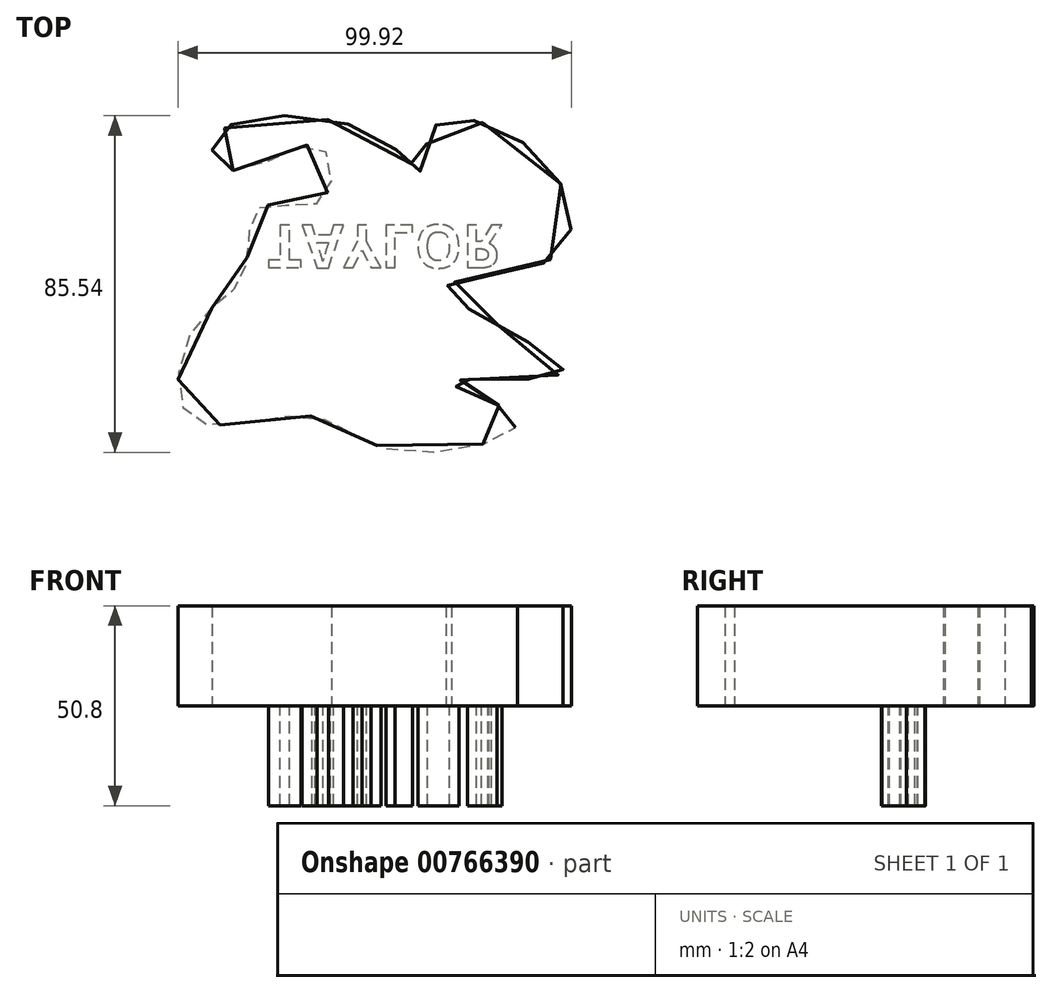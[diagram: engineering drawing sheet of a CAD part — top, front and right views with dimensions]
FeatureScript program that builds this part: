
annotation { "Feature Type Name" : "Feature", "Feature Type Description" : "" }
export const myFeature = defineFeature(function(context is Context, id is Id, definition is map)
    precondition{}
    {
        {
            var Q0;
            Q0=qCreatedBy(makeId("Top.planeOp"),FACE);
            var sketch = newSketch(context, id + "F0", { "sketchPlane" : qUnion([Q0])});
            skFitSpline(sketch, "E0", {"points": [v(-38.96, 34.8) * mm, v(-16.97, 40.86) * mm, v(-16.59, 27.02) * mm, v(-32.52, 25.12) * mm, v(-36.3, 8.25) * mm, v(-48.82, -5.02) * mm, v(-49.58, -28.16) * mm, v(-19.62, -27.59) * mm, v(2.94, -36.5) * mm, v(33.08, -28.53) * mm, v(16.59, -19.05) * mm, v(44.84, -16.21) * mm, v(15.26, 4.27) * mm, v(42.37, 12.6) * mm, v(39.15, 38.2) * mm, v(12.04, 45.79) * mm, v(9.39, 34.6) * mm, v(-3.89, 44.27) * mm, v(-43.51, 43.32) * mm, v(-38.96, 34.8) * mm]});
            skSolve(sketch);
        }
        {
            var Q0;
            Q0=makeQuery(id+"F0.imprint","IMPRINT",FACE,{"disambiguationData":[TD([[makeQuery(id+"F0.imprint","IMPRINT",EDGE,{"derivedFrom":sQuery(id+"F0.wireOp",EDGE,"E0")}),1.0]])]});
            extrude(context, id + "F1", {"entities" : qUnion([Q0]), "depth" : 25.4 * mm, "offsetDistance" : 25.4 * mm});
        }
        {
            var Q0;
            Q0=makeQuery(id+"F1.opExtrude","CAP_FACE",FACE,{"disambiguationData":[OSD([sQuery(id+"F0.wireOp",EDGE,"E0")])],"isStart":true});
            var sketch = newSketch(context, id + "F2", { "sketchPlane" : qUnion([Q0])});
            skText(sketch, "E1", { "text": "T", "fontName": "OpenSans-Bold.ttf"});
            const initialGuessF2  = {"E1": [-0.00813, -0.02705, 1, 0, 0.01205]};
            skSetInitialGuess(sketch, initialGuessF2);
            skSolve(sketch);
        }
        {
            var Q0;
            Q0 = qSketchRegion(id + "F2", true);
            extrude(context, id + "F3", {"entities" : qUnion([Q0]), "operationType" : NewBodyOperationType.ADD, "oppositeDirection" : true, "depth" : 25.4 * mm, "offsetDistance" : 25.4 * mm});
        }
        {
            var Q0;
            Q0=makeQuery(id+"F1.opExtrude","CAP_FACE",FACE,{"disambiguationData":[OSD([sQuery(id+"F0.wireOp",EDGE,"E0")])],"isStart":true});
            var sketch = newSketch(context, id + "F4", { "sketchPlane" : qUnion([Q0])});
            skText(sketch, "E2", { "text": "TAYLOR", "fontName": "OpenSans-Bold.ttf"});
            const initialGuessF4  = {"E2": [-0.03021, -0.02092, 1, 0, 0.01095]};
            skSetInitialGuess(sketch, initialGuessF4);
            skSolve(sketch);
        }
        {
            var Q0;
            Q0 = qSketchRegion(id + "F4", true);
            extrude(context, id + "F5", {"entities" : qUnion([Q0]), "operationType" : NewBodyOperationType.ADD, "depth" : 25.4 * mm, "offsetDistance" : 25.4 * mm});
        }
    });
